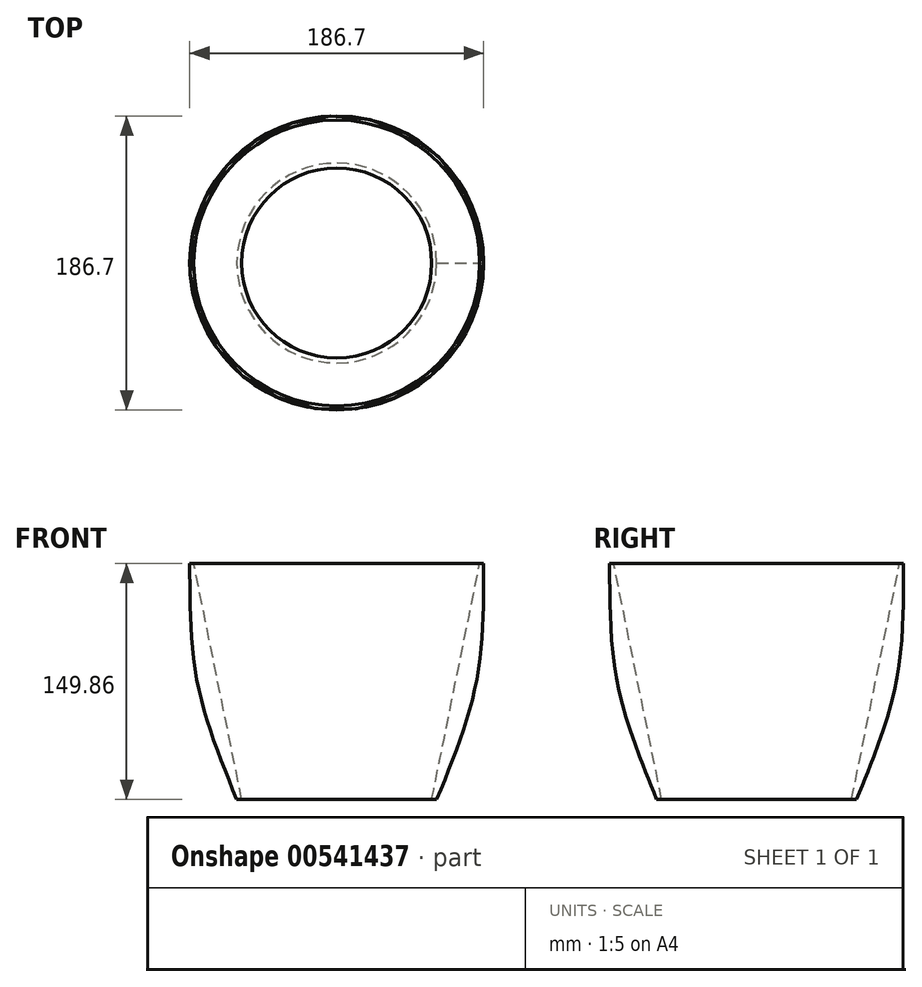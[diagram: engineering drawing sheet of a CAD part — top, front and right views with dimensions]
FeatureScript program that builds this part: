
annotation { "Feature Type Name" : "Feature", "Feature Type Description" : "" }
export const myFeature = defineFeature(function(context is Context, id is Id, definition is map)
    precondition{}
    {
        {
            var Q0;
            Q0=qCreatedBy(makeId("Top.planeOp"),FACE);
            cPlane(context, id + "F0", {"entities" : qUnion([Q0]), "cplaneType" : CPlaneType.OFFSET, "offset" : 114.3 * mm, "width" : 152.4 * mm, "height" : 152.4 * mm});
        }
        {
            var Q0;
            Q0=qCreatedBy(makeId("Top.planeOp"),FACE);
            cPlane(context, id + "F1", {"entities" : qUnion([Q0]), "cplaneType" : CPlaneType.OFFSET, "offset" : 264.16 * mm, "width" : 152.4 * mm, "height" : 152.4 * mm});
        }
        {
            var Q0;
            Q0=qCreatedBy(id+"F1.planeOp",FACE);
            var sketch = newSketch(context, id + "F2", { "sketchPlane" : qUnion([Q0])});
            skCircle(sketch, "E0", {"center": v(0, 0) * mm, "radius": 93.35 * mm});
            skSolve(sketch);
        }
        {
            var Q0;
            Q0=qCreatedBy(id+"F0.planeOp",FACE);
            var sketch = newSketch(context, id + "F3", { "sketchPlane" : qUnion([Q0])});
            skCircle(sketch, "E1", {"center": v(0, 0) * mm, "radius": 63.5 * mm});
            skSolve(sketch);
        }
        {
            var Q0;
            Q0=qCreatedBy(makeId("Top.planeOp"),FACE);
            cPlane(context, id + "F4", {"entities" : qUnion([Q0]), "cplaneType" : CPlaneType.OFFSET, "offset" : 190.5 * mm, "width" : 152.4 * mm, "height" : 152.4 * mm});
        }
        {
            var Q0;
            Q0=qCreatedBy(id+"F4.planeOp",FACE);
            var sketch = newSketch(context, id + "F5", { "sketchPlane" : qUnion([Q0])});
            skCircle(sketch, "E2", {"center": v(0, 0) * mm, "radius": 88.9 * mm});
            skSolve(sketch);
        }
        {
            var Q0;
            Q0=makeQuery(id+"F3.imprint","IMPRINT",FACE,{"disambiguationData":[TD([[makeQuery(id+"F3.imprint","IMPRINT",EDGE,{"derivedFrom":sQuery(id+"F3.wireOp",EDGE,"E1")}),1.0]])]});
            var Q1;
            Q1=makeQuery(id+"F5.imprint","IMPRINT",FACE,{"disambiguationData":[TD([[makeQuery(id+"F5.imprint","IMPRINT",EDGE,{"derivedFrom":sQuery(id+"F5.wireOp",EDGE,"E2")}),1.0]])]});
            var Q2;
            Q2=makeQuery(id+"F2.imprint","IMPRINT",FACE,{"disambiguationData":[TD([[makeQuery(id+"F2.imprint","IMPRINT",EDGE,{"derivedFrom":sQuery(id+"F2.wireOp",EDGE,"E0")}),1.0]])]});
            loft(context, id + "F6", {"sheetProfilesArray" : [{ "sheetProfileEntities" : qUnion([Q0]) }, { "sheetProfileEntities" : qUnion([Q1]) }, { "sheetProfileEntities" : qUnion([Q2]) }]});
        }
        {
            var Q0;
            Q0=qCreatedBy(id+"F1.planeOp",FACE);
            var sketch = newSketch(context, id + "F7", { "sketchPlane" : qUnion([Q0])});
            skCircle(sketch, "E3", {"center": v(0, 0) * mm, "radius": 90.8 * mm});
            skSolve(sketch);
        }
        {
            var Q0;
            Q0=qCreatedBy(id+"F0.planeOp",FACE);
            var sketch = newSketch(context, id + "F8", { "sketchPlane" : qUnion([Q0])});
            skCircle(sketch, "E4", {"center": v(0, 0) * mm, "radius": 60.33 * mm});
            skSolve(sketch);
        }
        {
            var Q1;
            Q1=makeQuery(id+"F8.imprint","IMPRINT",FACE,{"disambiguationData":[TD([[makeQuery(id+"F8.imprint","IMPRINT",EDGE,{"derivedFrom":sQuery(id+"F8.wireOp",EDGE,"E4")}),1.0]])]});
            var Q2;
            Q2=makeQuery(id+"F7.imprint","IMPRINT",FACE,{"disambiguationData":[TD([[makeQuery(id+"F7.imprint","IMPRINT",EDGE,{"derivedFrom":sQuery(id+"F7.wireOp",EDGE,"E3")}),1.0]])]});
            loft(context, id + "F9", {"operationType" : NewBodyOperationType.REMOVE, "sheetProfilesArray" : [{ "sheetProfileEntities" : qUnion([Q1]) }, { "sheetProfileEntities" : qUnion([Q2]) }]});
        }
    });
